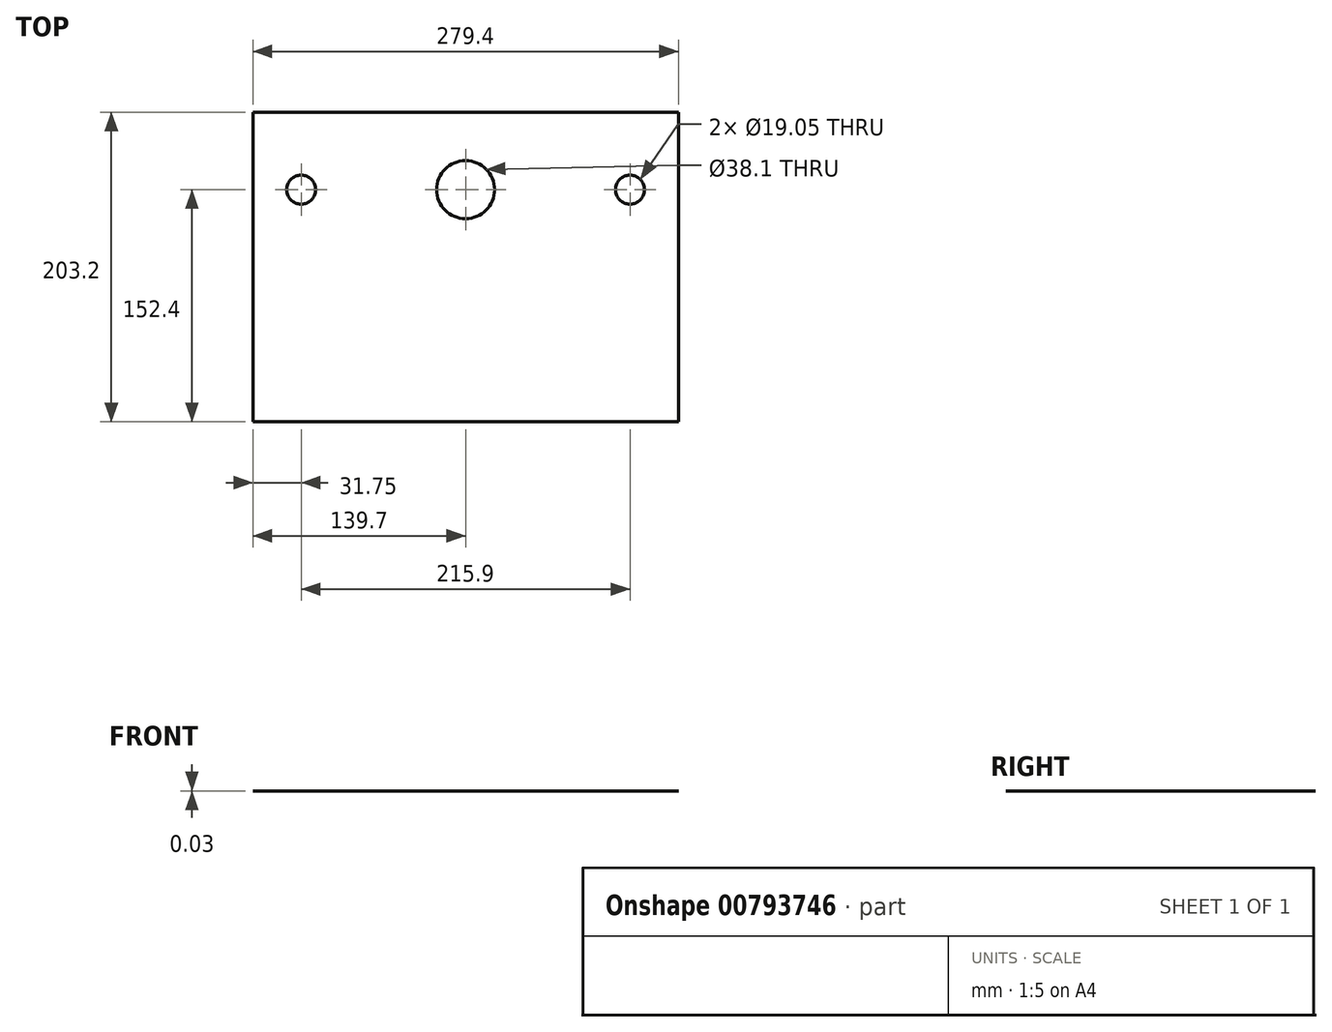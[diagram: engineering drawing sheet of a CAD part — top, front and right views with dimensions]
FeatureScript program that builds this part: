
annotation { "Feature Type Name" : "Feature", "Feature Type Description" : "" }
export const myFeature = defineFeature(function(context is Context, id is Id, definition is map)
    precondition{}
    {
        {
            var Q0;
            Q0=qCreatedBy(makeId("Top.planeOp"),FACE);
            var sketch = newSketch(context, id + "F0", { "sketchPlane" : qUnion([Q0])});
            skLineSegment(sketch, "E0.bottom", {"start": v(0, 0) * mm, "end": v(279.4, 0) * mm});
            skLineSegment(sketch, "E0.top", {"start": v(0, 203.2) * mm, "end": v(279.4, 203.2) * mm});
            skLineSegment(sketch, "E0.left", {"start": v(0, 0) * mm, "end": v(0, 203.2) * mm});
            skLineSegment(sketch, "E0.right", {"start": v(279.4, 0) * mm, "end": v(279.4, 203.2) * mm});
            skSolve(sketch);
        }
        {
            var Q0;
            Q0 = qSketchRegion(id + "F0", true);
            extrude(context, id + "F1", {"entities" : qUnion([Q0]), "depth" : 7 / 203.2 * mm, "offsetDistance" : 25.4 * mm});
        }
        {
            var Q0;
            Q0=makeQuery(id+"F1.opExtrude","CAP_FACE",FACE,{"disambiguationData":[OSD([sQuery(id+"F0.wireOp",EDGE,"E0.bottom"),sQuery(id+"F0.wireOp",EDGE,"E0.top"),sQuery(id+"F0.wireOp",EDGE,"E0.left"),sQuery(id+"F0.wireOp",EDGE,"E0.right")])],"isStart":false});
            var sketch = newSketch(context, id + "F2", { "sketchPlane" : qUnion([Q0])});
            skCircle(sketch, "E1", {"center": v(139.7, 152.4) * mm, "radius": 19.05 * mm});
            skCircle(sketch, "E2", {"center": v(247.65, 152.4) * mm, "radius": 9.53 * mm});
            skCircle(sketch, "E3", {"center": v(31.75, 152.4) * mm, "radius": 9.53 * mm});
            skSolve(sketch);
        }
        {
            var Q0;
            Q0 = qSketchRegion(id + "F2", true);
            extrude(context, id + "F3", {"entities" : qUnion([Q0]), "operationType" : NewBodyOperationType.REMOVE, "oppositeDirection" : true, "depth" : 7 / 203.2 * mm, "offsetDistance" : 25.4 * mm});
        }
    });
